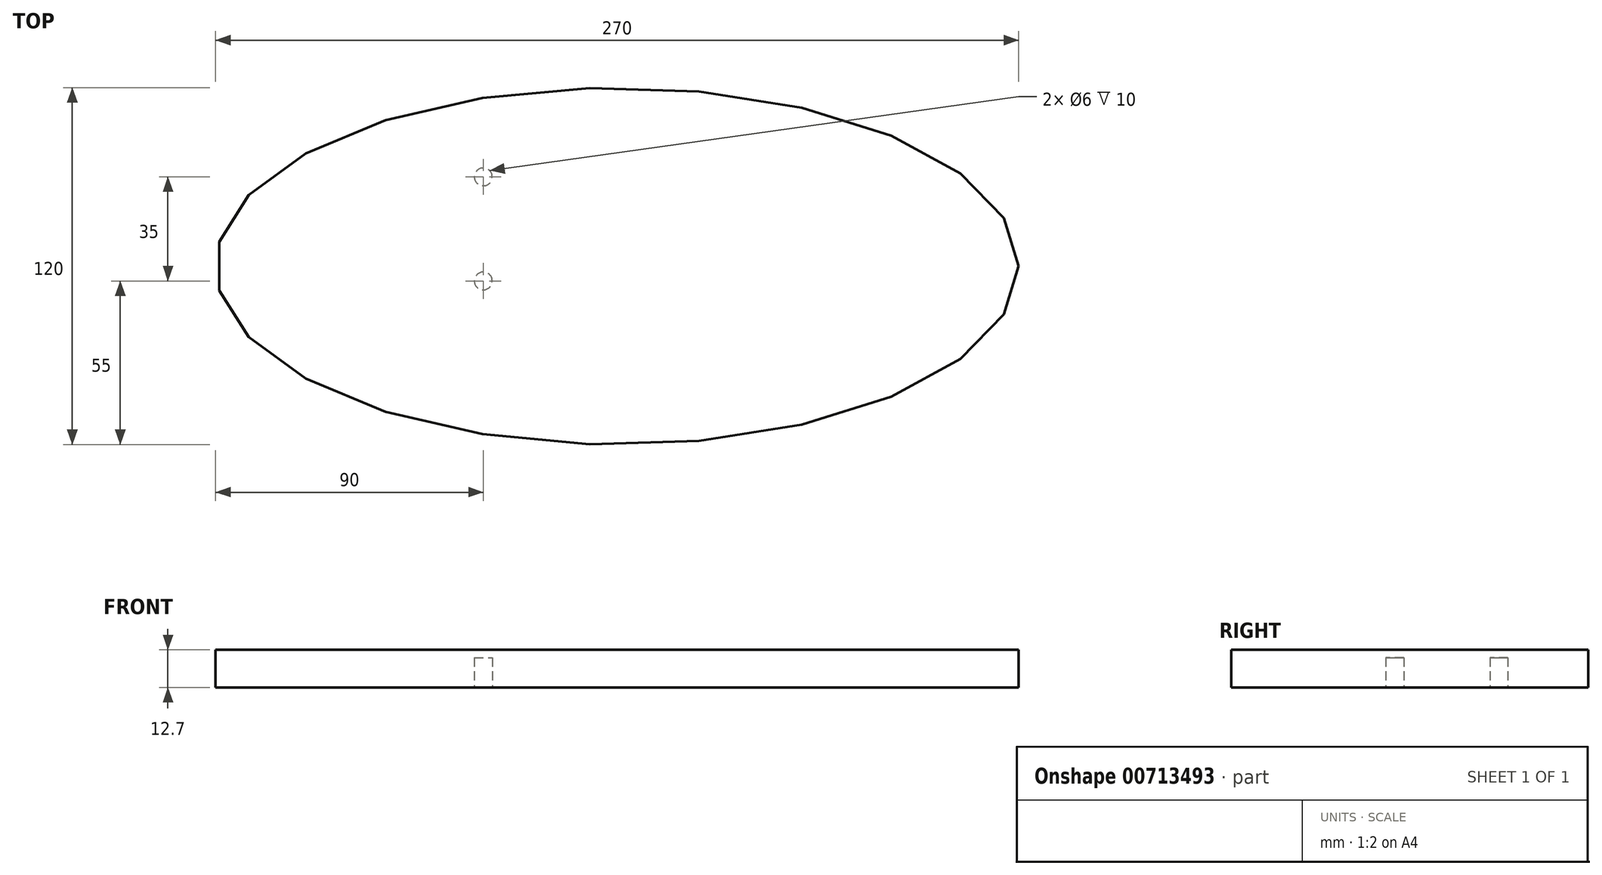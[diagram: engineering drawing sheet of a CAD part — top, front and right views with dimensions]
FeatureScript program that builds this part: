
annotation { "Feature Type Name" : "Feature", "Feature Type Description" : "" }
export const myFeature = defineFeature(function(context is Context, id is Id, definition is map)
    precondition{}
    {
        {
            var Q0;
            Q0=qCreatedBy(makeId("Top.planeOp"),FACE);
            var sketch = newSketch(context, id + "F0", { "sketchPlane" : qUnion([Q0])});
            skEllipse(sketch, "E0", {"center": v(0, 0) * mm, "majorRadius": 135 * mm, "minorRadius": 60 * mm, "majorAxis": v(1, 0)});
            skSolve(sketch);
        }
        {
            var Q0;
            Q0 = qSketchRegion(id + "F0", true);
            extrude(context, id + "F1", {"entities" : qUnion([Q0]), "depth" : 12.7 * mm, "offsetDistance" : 25 * mm});
        }
        {
            var Q0;
            Q0=makeQuery(id+"F1.opExtrude","CAP_FACE",FACE,{"disambiguationData":[OSD([sQuery(id+"F0.wireOp",EDGE,"E0")])],"isStart":true});
            var sketch = newSketch(context, id + "F2", { "sketchPlane" : qUnion([Q0])});
            skCircle(sketch, "E1", {"center": v(-45, -30) * mm, "radius": 3 * mm});
            skCircle(sketch, "E2", {"center": v(-45, 5) * mm, "radius": 3 * mm});
            skLineSegment(sketch, "E3", {"start": v(-45, -30) * mm, "end": v(-45, 5) * mm, "construction": true});
            skLineSegment(sketch, "E4", {"start": v(0, 0) * mm, "end": v(-135, 0) * mm, "construction": true});
            skSolve(sketch);
        }
        {
            var Q0;
            Q0 = qSketchRegion(id + "F2", true);
            extrude(context, id + "F3", {"entities" : qUnion([Q0]), "operationType" : NewBodyOperationType.REMOVE, "oppositeDirection" : true, "depth" : 10 * mm, "offsetDistance" : 25 * mm});
        }
    });
